# Revit family: НЕВАТОМ_Вентилятор VKPN EC, версия 1
name_source: partatom
category: Оборудование
revit_build: Autodesk Revit 2017 (Build: 20170118_1100(x64)
units: mm (PartAtom-declared; Revit-internal decimal feet)

## family parameters
Всегда вертикально = Да
На основе рабочей плоскости = Нет
Общий = Нет
При загрузке вырезать с полостями = Нет
Размер круглого соединителя = Использовать диаметр
Тип детали = Вставляется
Точка расчета площади = Нет

## types (12) — shared parameters
ADSK_Единица измерения = шт.
ADSK_Завод-изготовитель = НЕВАТОМ
ADSK_Количество = 1
ADSK_Материал наименование = Оцинкованная сталь
ADSK_Наименование = Вентилятор канальный прямоугольный с назад загнутыми лопатками
Nevatom_URL = https://t.me
Ключевая пометка = Вентиляция
Коэффициент расхода = 1
Крышка = СВМПЭ, белый
Материал = Сталь серая

## per-type parameters (varying)
| type | 1 | 2 | A | ADSK_Марка | ADSK_Масса | ADSK_Масса_Текст | ADSK_Напряжение | ADSK_Полная мощность | ADSK_Размер_Высота | ADSK_Размер_Длина | ADSK_Размер_Ширина | ADSK_Расход воздуха | ADSK_Ток | ADSK_Частота вращения вентилятора | B | E | F | H | L | Полное давление |
| VKPN EC 400-200/22-6E | 260 мм | 60 мм | 400 мм | VKPN EC 400-200/22-6E | 11.06 | 11.06 кг | 230 В | 0 кВт | 283 мм | 446 мм | 450 мм | 1140.0 м³/ч | 1 А | 3350 | 200 мм | 446 мм | 263 мм | 283 мм | 450 мм | 640.0 Па |
| VKPN EC 800-500/56-8D | 520 мм | 120 мм | 800 мм | VKPN EC 800-500/56-8D | 62.3 | 62.3 кг | 380 В | 4 кВт | 609 мм | 854 мм | 830 мм | 12900.0 м³/ч | 6 А | 1830 | 500 мм | 854 мм | 557 мм | 609 мм | 830 мм | 1110.0 Па |
| VKPN EC 500-250/25-2E | 325 мм | 75 мм | 500 мм | VKPN EC 500-250/25-2E | 14.77 | 14.77 | 230 В | 0 кВт | 333 мм | 546 мм | 490 мм | 1380.0 м³/ч | 2 А | 2800 | 250 мм | 546 мм | 313 мм | 333 мм | 490 мм | 530.0 Па |
| VKPN EC 500-300/25-6E | 325 мм | 75 мм | 500 мм | VKPN EC 500-300/25-6E | 18.1 | 18.1 кг | 230 В | 1 кВт | 389 мм | 546 мм | 530 мм | 3050.0 м³/ч | 2 А | 3100 | 300 мм | 546 мм | 363 мм | 389 мм | 530 мм | 845.0 Па |
| VKPN EC 600-300/25-6E | 390 мм | 90 мм | 600 мм | VKPN EC 600-300/25-6E | 21.7 | 21.7 кг | 230 В | 1 кВт | 389 мм | 646 мм | 640 мм | 2900.0 м³/ч | 2 А | 3100 | 300 мм | 646 мм | 363 мм | 389 мм | 640 мм | 830.0 Па |
| VKPN EC  600-300/28-6D | 390 мм | 90 мм | 600 мм | VKPN EC 600-300/28-6D | 21.7 | 21.7 кг | 380 В | 1 кВт | 406 мм | 646 мм | 640 мм | 3980.0 м³/ч | 2 А | 3270 | 300 мм | 646 мм | 363 мм | 406 мм | 640 мм | 1170.0 Па |
| VKPN EC 600-350/28-6D | 390 мм | 90 мм | 600 мм | VKPN EC 600-350/28-6D | 28.2 | 28.2 кг | 380 В | 1 кВт | 456 мм | 646 мм | 705 мм | 4350.0 м³/ч | 2 А | 3270 | 350 мм | 646 мм | 413 мм | 456 мм | 705 мм | 1225.0 Па |
| VKPN EC 700-400/35-8D | 455 мм | 105 мм | 700 мм | VKPN EC 700-400/35-8D | 42.8 | 42.8 кг | 380 В | 2 кВт | 487 мм | 754 мм | 787 мм | 6500.0 м³/ч | 3 А | 2530 | 400 мм | 754 мм | 457 мм | 487 мм | 787 мм | 1050.0 Па |
| VKPN EC 700-400/28-6D | 455 мм | 105 мм | 700 мм | VKPN EC 700-400/28-6D | 42.8 | 44.6 кг | 380 В | 1 кВт | 505 мм | 754 мм | 787 мм | 4480.0 м³/ч | 2 А | 3270 | 400 мм | 754 мм | 457 мм | 505 мм | 787 мм | 1130.0 Па |
| VKPN EC 900-500/56-8D | 585 мм | 135 мм | 900 мм | VKPN EC 900-500/56-8D | 66.5 | 66.5 кг | 380 В | 4 кВт | 609 мм | 954 мм | 830 мм | 12900.0 м³/ч | 6 А | 1830 | 500 мм | 954 мм | 557 мм | 609 мм | 830 мм | 1110.0 Па |
| VKPN EC 600-350/35-8D | 390 мм | 90 мм | 600 мм | VKPN EC 600-350/35-8D | 28.2 | 28.2 кг | 380 В | 1 кВт | 448 мм | 646 мм | 705 мм | 5850.0 м³/ч | 2 А | 2200 | 350 мм | 646 мм | 413 мм | 448 мм | 705 мм | 920.0 Па |
| VKPN EC 1000-500/56-8D | 650 мм | 150 мм | 1000 мм | VKPN EC 1000-500/56-8D | 66.5 | 73.3 | 380 В | 4 кВт | 609 мм | 1054 мм | 1020 мм | 12900.0 м³/ч | 6 А | 1830 | 500 мм | 1054 мм | 557 мм | 609 мм | 1020 мм | 1110.0 Па |
